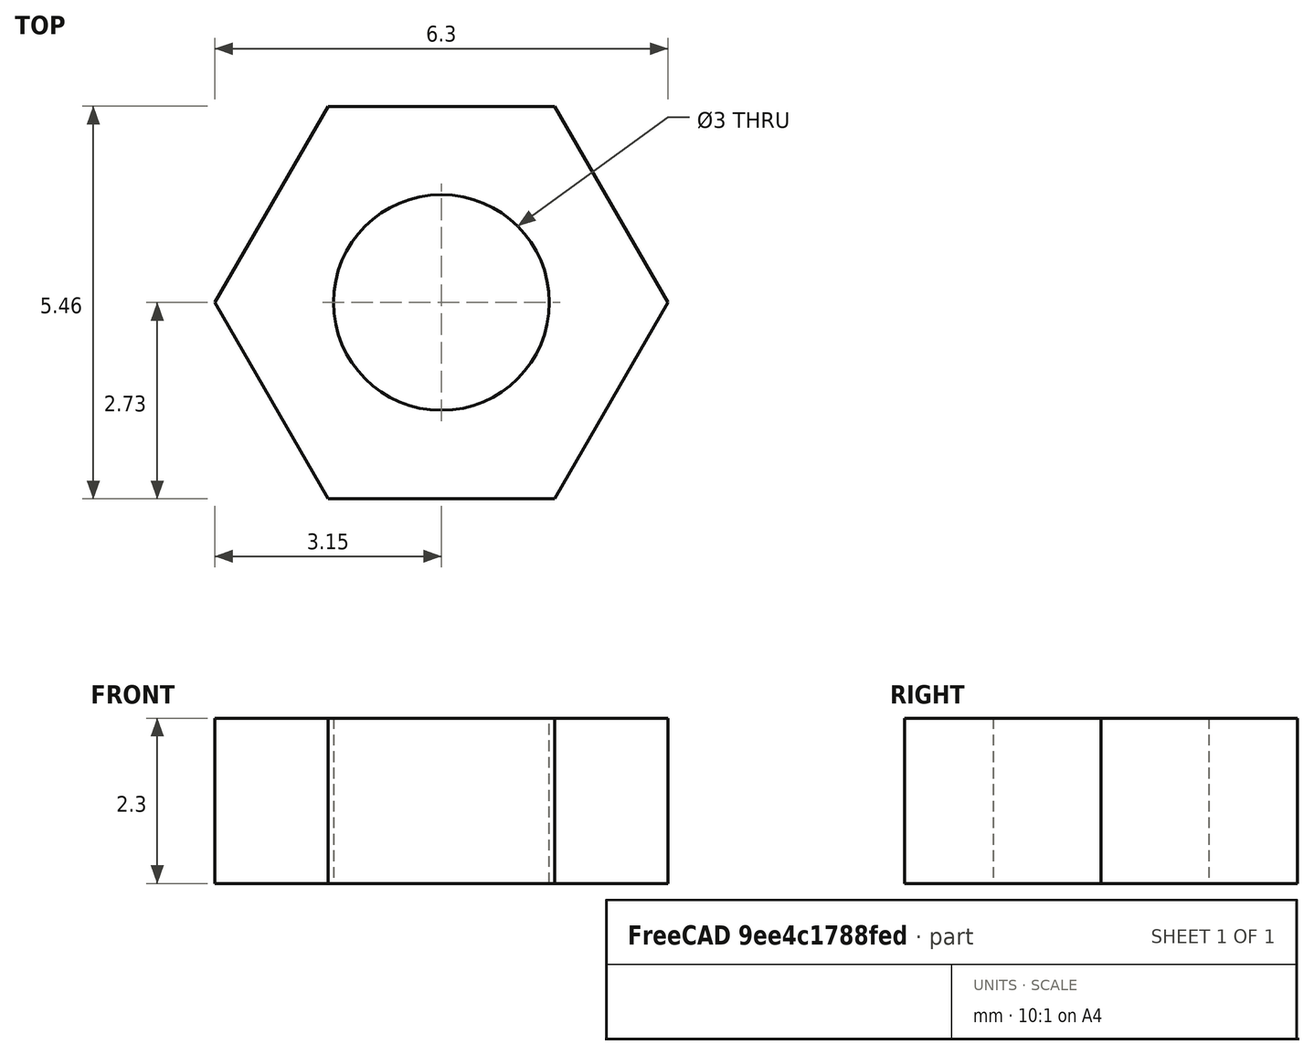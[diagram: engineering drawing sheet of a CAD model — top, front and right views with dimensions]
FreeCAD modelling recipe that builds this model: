
FCSTD DOCUMENT  (FreeCAD 0.16R6706 (Git))
Label: nut
License: All rights reserved
LicenseURL: http://en.wikipedia.org/wiki/All_rights_reserved
objects: Sketcher::SketchObject×1, PartDesign::Pad×1
note: 3 computed .brp shape members not serialized (recipe doc carries the construction recipe); baked Part::Feature solids carry a one-line shape summary decoded from their .brp

FEATURE [Sketcher::SketchObject] Sketch
  sketch-geometry (8):
    g0: LineSegment StartX=1.575 StartY=-2.72798 StartZ=0 EndX=3.15 EndY=0 EndZ=0
    g1: LineSegment StartX=3.15 StartY=0 StartZ=0 EndX=1.575 EndY=2.72798 EndZ=0
    g2: LineSegment StartX=1.575 StartY=2.72798 StartZ=0 EndX=-1.575 EndY=2.72798 EndZ=0
    g3: LineSegment StartX=-1.575 StartY=2.72798 StartZ=0 EndX=-3.15 EndY=0 EndZ=0
    g4: LineSegment StartX=-3.15 StartY=0 StartZ=0 EndX=-1.575 EndY=-2.72798 EndZ=0
    g5: LineSegment StartX=-1.575 StartY=-2.72798 StartZ=0 EndX=1.575 EndY=-2.72798 EndZ=0
    g6: Circle [constr] CenterX=0 CenterY=0 CenterZ=0 NormalX=0 NormalY=0 NormalZ=1 Radius=3.15
    g7: Circle CenterX=0 CenterY=0 CenterZ=0 NormalX=0 NormalY=0 NormalZ=1 Radius=1.5
  constraints (18):
    c: Coincident(g0,g1)
    c: Coincident(g1,g2)
    c: Coincident(g2,g3)
    c: Coincident(g3,g4)
    c: Coincident(g4,g5)
    c: Coincident(g5,g0)
    c: Equal(g0, g1-g5) x5
    c: PointOnObject(g0,g6)
    c: PointOnObject(g1,g6)
    c: PointOnObject(g2,g6)
    c: PointOnObject(g3,g6)
    c: PointOnObject(g4,g6)
    c: PointOnObject(g5,g6)
    c: Coincident(g6,g-1)
    c: Horizontal(g5)
    c: Radius(g6) = 3.15
    c: Coincident(g7,g-1)
    c: Radius(g7) = 1.5
FEATURE [PartDesign::Pad] Pad
  Length = 2.3
  Length2 = 100
  Sketch = -> Sketch
  Type = 0
